# Revit family: Power-ModularDevices-GEWISS-90RCD-MDC100_2P
name_source: partatom
category: Apparecchi elettrici
revit_build: Autodesk Revit MEP 2016 (Build: 20150220_1215(x64)
units: mm (PartAtom-declared; Revit-internal decimal feet)

## family parameters
Condiviso = Sì
Host = Superficie
Mantenere orientamento annotazione = Sì
Numero OmniClass = 23.80.30.14
Punto di calcolo locali = Sì
Quota connettore circolare = Usa diametro
Taglio con vuoti quando caricato = No
Tipo di parte = Normale
Titolo OmniClass = Power Distribution

## types (1)
- Power-ModularDevices-GEWISS-90RCD-MDC100_2P
    Altezza = 85 mm  [stored 0.278871 ft]
    Assembly position: = Any
    Auxiliaries compatibility = Yes
    Breaking capacity EN 60947-2 (Ics) = 75% Icu
    Breaking capacity EN 60947-2 230V (Icu) = 10KA
    Breaking capacity EN 61009-1 (Ics) = 0.75 x Icn
    Breaking capacity EN 61009-1 230V (Icn) = 10000A
    Carico apparente = 0 VA
    Catalogue = POWER
    Catalogue Range = 90 RCD
    Curve = B
    Description = RCCB WITH OVERCURRENT PROTECTION
    Descrizione = COMPACT RCBO 2P B13 10KA AIR/0,03 2M
    Double connection = YES (only down stream)
    EAN code = 8011564762466
    Electrical endurance = 10000
    Electrocod = 1413
    Finitura = GW - grigio chiaro
    IDF = 5f67d62a-e56c-4c8a-898d-2f42b0347686
    IDT = 714fe196-de76-41c7-887b-bffd1e399468
    Idn = 30MA
    Immagine tipo = GW94006.jpg
    Insulation voltage = 500V
    Interuttore = GW - grigio scuro
    Label = MDC 100
    Larghezza = 36 mm  [stored 0.11811 ft]
    Level of immunity (8/20 µs) = 3000A
    Mechanical endurance = 20.000
    Modello = GW95841
    No. modules = 2
    No. of modules EN 50022 = 2
    No. of poles = 2P
    Number of poles = 2P
    Numero di poli_ = 2
    Operating temperature = -25 +40 °C
    Overvoltage category = III
    Parti incassate = Sì
    Precision = 30 mA
    Produttore = GEWISS S.p.A.
    Prospetto di default = 1219 mm
    Rated current (In) = 13A
    Rated current: = 13A
    Rated frequency (Hz) = 50/60 Hz
    Rated impulse withstand voltage = 4KV
    Rated insulation voltage (Ui) = 500V
    Rated residual operating current = 30 mA
    Rated tightening torque = 2 Nm
    Rated voltage = 230V
    Rated voltage (EN/IEC 61009-1, 61009-2-1) = 230/240 V
    ReStart compatibility = Yes
    SEO = RCCB
    Section flexible cable = <=1x35 - <=2x16 - <=1x16+2x10 mm²
    Section rigid cable = <=1x35 - <=2x16 - <=1x16+2x10 mm²
    Simbolo tipo = Sì
    Spessore = 150 mm
    Standard = EN 61009-1
    Standard; = IEC/EN 61009-1, IEC/EN 61009-2-1
    Stocking temperature = -40 +70 °C
    Technical sheet = https://www.gewiss.com
    Type = A(IR)
    Type: = A[IR]
    URL = https://www.gewiss.com
    Version file RFA = 19.0
    Voltaggio = 230 V

note: [stored X ft] marks values corroborated as IEEE doubles in the binary element streams (Revit-internal decimal feet)

## geometry (parser evidence)
native form markers: Sweep x2
no freeform markers — native parametric forms only
